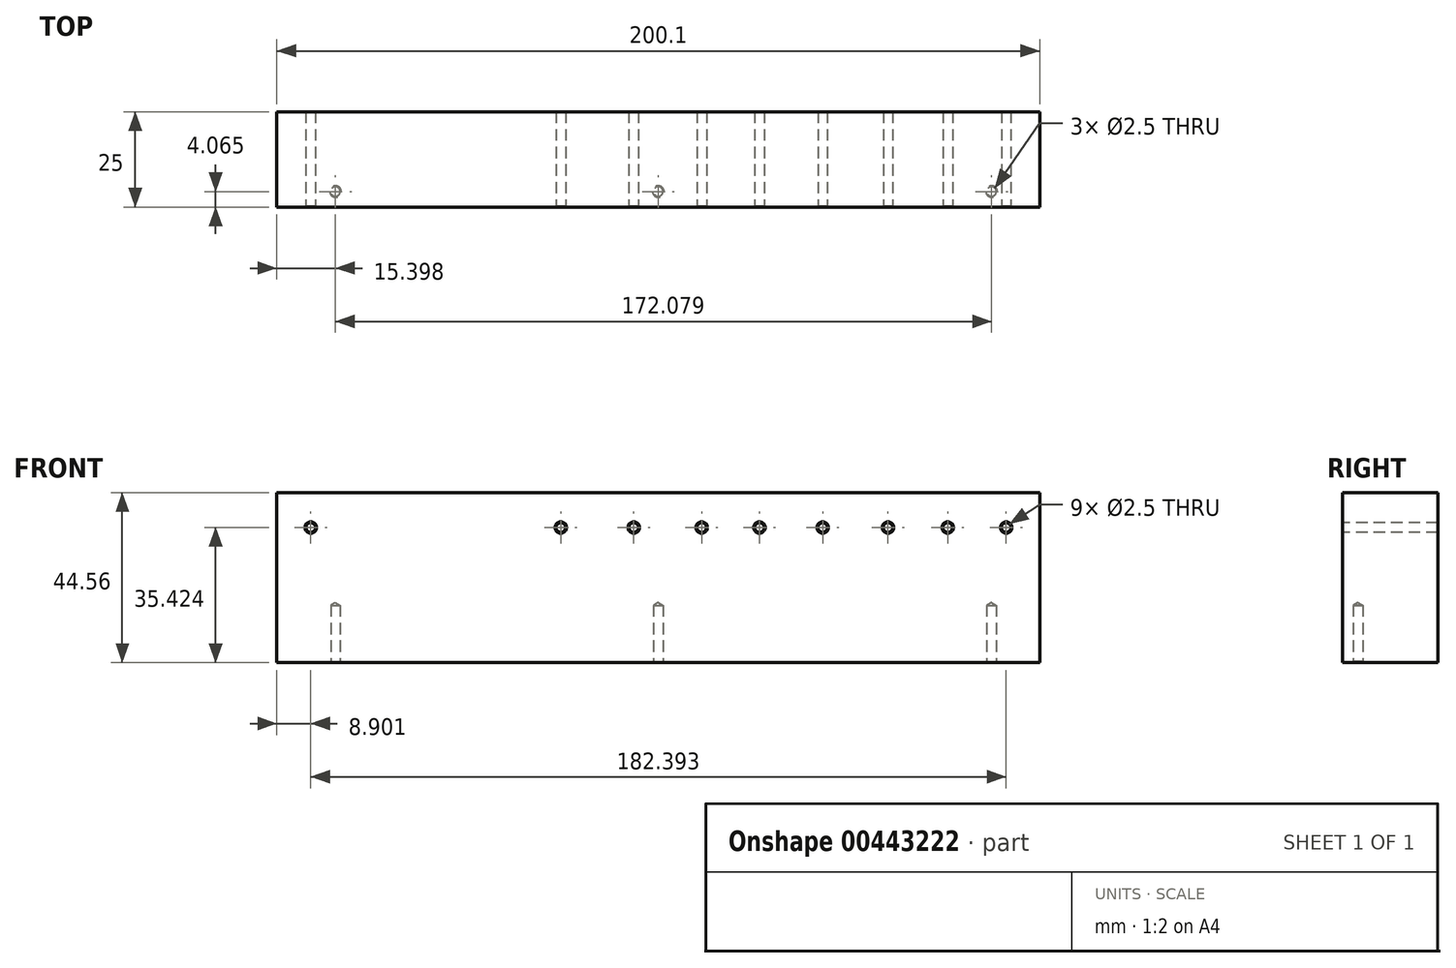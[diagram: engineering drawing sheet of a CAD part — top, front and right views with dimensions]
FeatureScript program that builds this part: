
annotation { "Feature Type Name" : "Feature", "Feature Type Description" : "" }
export const myFeature = defineFeature(function(context is Context, id is Id, definition is map)
    precondition{}
    {
        {
            var Q0;
            Q0=qCreatedBy(makeId("Front.planeOp"),FACE);
            var sketch = newSketch(context, id + "F0", { "sketchPlane" : qUnion([Q0])});
            skLineSegment(sketch, "E0.bottom", {"start": v(100.05, 22.28) * mm, "end": v(-100.05, 22.28) * mm});
            skLineSegment(sketch, "E0.top", {"start": v(100.05, -22.28) * mm, "end": v(-100.05, -22.28) * mm});
            skLineSegment(sketch, "E0.left", {"start": v(100.05, 22.28) * mm, "end": v(100.05, -22.28) * mm});
            skLineSegment(sketch, "E0.right", {"start": v(-100.05, 22.28) * mm, "end": v(-100.05, -22.28) * mm});
            skPoint(sketch, "E0.middle", {"position": v(0, 0) * mm});
            skPoint(sketch, "E1", {"position": v(92.54, 16.75) * mm});
            skPoint(sketch, "E2", {"position": v(-92.68, 16.75) * mm});
            skPoint(sketch, "E3", {"position": v(-77.18, 16.75) * mm});
            skPoint(sketch, "E4", {"position": v(-61.32, 16.75) * mm});
            skPoint(sketch, "E5", {"position": v(-45.81, 16.75) * mm});
            skPoint(sketch, "E6", {"position": v(-31, 16.75) * mm});
            skPoint(sketch, "E7", {"position": v(-16.03, 16.75) * mm});
            skPoint(sketch, "E8", {"position": v(0, 16.75) * mm});
            skPoint(sketch, "E9", {"position": v(17.43, 16.75) * mm});
            skSolve(sketch);
        }
        {
            var Q0;
            Q0=makeQuery(id+"F0.imprint","IMPRINT",FACE,{"disambiguationData":[TD([[makeQuery(id+"F0.imprint","IMPRINT",EDGE,{"derivedFrom":sQuery(id+"F0.wireOp",EDGE,"E0.bottom")}),1.0]])]});
            extrude(context, id + "F1", {"entities" : qUnion([Q0]), "depth" : 25 * mm});
        }
        {
            var Q0;
            Q0=makeQuery(id+"F1.opExtrude","CAP_FACE",FACE,{"disambiguationData":[OSD([sQuery(id+"F0.wireOp",EDGE,"E0.bottom"),sQuery(id+"F0.wireOp",EDGE,"E0.top"),sQuery(id+"F0.wireOp",EDGE,"E0.left"),sQuery(id+"F0.wireOp",EDGE,"E0.right")])],"isStart":false});
            var sketch = newSketch(context, id + "F2", { "sketchPlane" : qUnion([Q0])});
            skPoint(sketch, "E10", {"position": v(-91.15, 13.14) * mm});
            skPoint(sketch, "E11", {"position": v(91.24, 13.14) * mm});
            skPoint(sketch, "E12", {"position": v(75.92, 13.14) * mm});
            skPoint(sketch, "E13", {"position": v(60.24, 13.14) * mm});
            skPoint(sketch, "E14", {"position": v(43.12, 13.14) * mm});
            skPoint(sketch, "E15", {"position": v(26.54, 13.14) * mm});
            skPoint(sketch, "E16", {"position": v(11.4, 13.14) * mm});
            skPoint(sketch, "E17", {"position": v(-6.44, 13.14) * mm});
            skPoint(sketch, "E18", {"position": v(-25.55, 13.14) * mm});
            skSolve(sketch);
        }
        {
            var Q0;
            Q0=sQuery(id+"F2.wireOp",VERTEX,"E10");
            var Q1;
            Q1=sQuery(id+"F2.wireOp",VERTEX,"E18");
            var Q2;
            Q2=sQuery(id+"F2.wireOp",VERTEX,"E17");
            var Q3;
            Q3=sQuery(id+"F2.wireOp",VERTEX,"E16");
            var Q4;
            Q4=sQuery(id+"F2.wireOp",VERTEX,"E15");
            var Q5;
            Q5=sQuery(id+"F2.wireOp",VERTEX,"E14");
            var Q6;
            Q6=sQuery(id+"F2.wireOp",VERTEX,"E13");
            var Q7;
            Q7=sQuery(id+"F2.wireOp",VERTEX,"E12");
            var Q8;
            Q8=sQuery(id+"F2.wireOp",VERTEX,"E11");
            var Q9;
            Q9=makeQuery(id+"F1.opExtrude","SWEPT_BODY",BODY,{"disambiguationData":[OSD([sQuery(id+"F0.wireOp",EDGE,"E0.bottom"),sQuery(id+"F0.wireOp",EDGE,"E0.top"),sQuery(id+"F0.wireOp",EDGE,"E0.left"),sQuery(id+"F0.wireOp",EDGE,"E0.right")])]});
            hole(context, id + "F3", {"style" : HoleStyle.C_SINK, "endStyle" : HoleEndStyle.THROUGH, "holeDiameter" : 2.5 * mm, "cSinkDiameter" : 3 * mm, "cSinkAngle" : 90 * degree, "isTappedThrough" : true, "tappedDepth" : 12 * mm, "tapClearance" : 3, "startFromSketch" : true, "locations" : qUnion([Q0, Q1, Q2, Q3, Q4, Q5, Q6, Q7, Q8]), "scope" : qUnion([Q9])});
        }
        {
            var Q0;
            Q0=makeQuery(id+"F1.opExtrude","SWEPT_FACE",FACE,{"disambiguationData":[OSD([sQuery(id+"F0.wireOp",EDGE,"E0.top")])]});
            var sketch = newSketch(context, id + "F4", { "sketchPlane" : qUnion([Q0])});
            skPoint(sketch, "E19", {"position": v(-84.65, 20.94) * mm});
            skPoint(sketch, "E20", {"position": v(0, 20.94) * mm});
            skPoint(sketch, "E21", {"position": v(87.43, 20.94) * mm});
            skSolve(sketch);
        }
        {
            var Q0;
            Q0=sQuery(id+"F4.wireOp",VERTEX,"E21");
            var Q1;
            Q1=sQuery(id+"F4.wireOp",VERTEX,"E20");
            var Q2;
            Q2=sQuery(id+"F4.wireOp",VERTEX,"E19");
            var Q3;
            Q3=makeQuery(id+"F1.opExtrude","SWEPT_BODY",BODY,{"disambiguationData":[OSD([sQuery(id+"F0.wireOp",EDGE,"E0.bottom"),sQuery(id+"F0.wireOp",EDGE,"E0.top"),sQuery(id+"F0.wireOp",EDGE,"E0.left"),sQuery(id+"F0.wireOp",EDGE,"E0.right")])]});
            hole(context, id + "F5", {"style" : HoleStyle.C_SINK, "endStyle" : HoleEndStyle.BLIND, "holeDiameter" : 2.5 * mm, "cSinkDiameter" : 3 * mm, "cSinkAngle" : 90 * degree, "holeDepth" : 15 * mm, "isTappedThrough" : true, "tappedDepth" : 12 * mm, "tapClearance" : 3, "startFromSketch" : true, "locations" : qUnion([Q0, Q1, Q2]), "scope" : qUnion([Q3])});
        }
    });
